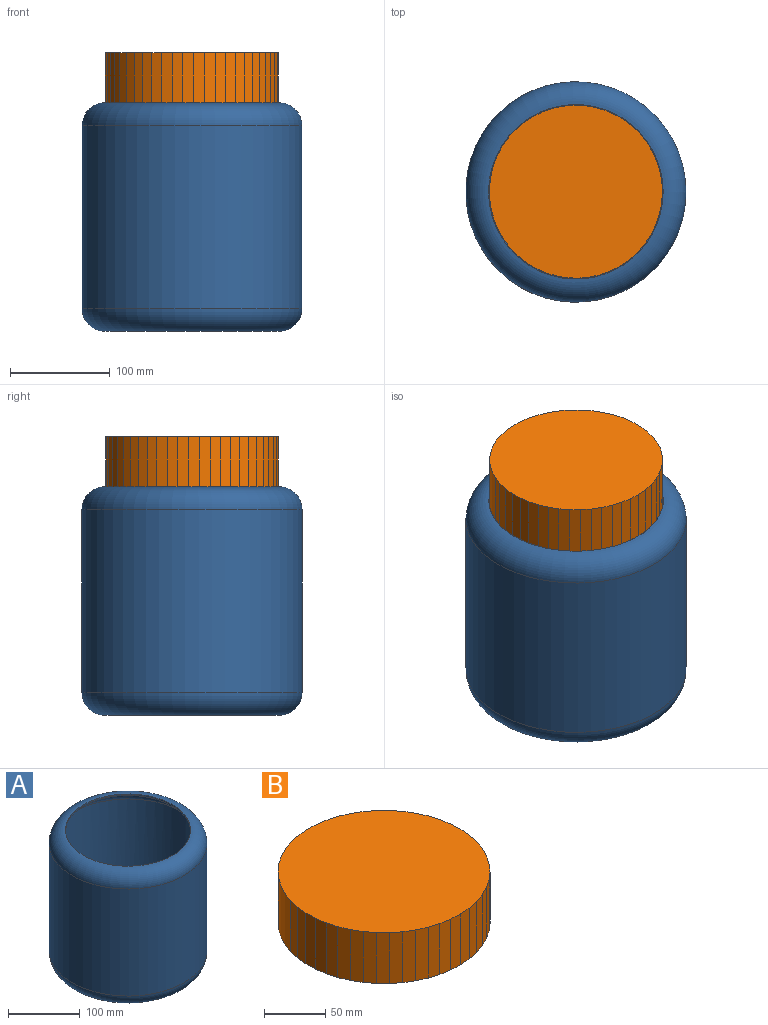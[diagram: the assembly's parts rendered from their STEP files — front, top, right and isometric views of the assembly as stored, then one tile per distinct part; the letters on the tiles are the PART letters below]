
ASSEMBLY  parts=2 mates=1
PART A: 9 faces, bbox 238.4x238.4x228.6 mm
  f0: cylinder r=110.11mm len=220.23mm, axis (0,0,-1), area 126529.7mm2, adj f2,f3
  f1: plane 174.51x174.51mm, normal (0,0,-1), area 23918.3mm2, adj f3
  f2: torus R=87.25mm, axis (0,0,1), area 22969.9mm2, adj f0,f4
  f3: torus R=87.25mm, axis (0,0,1), area 22969.9mm2, adj f0,f1
  f4: cylinder r=87.25mm len=174.51mm, axis (0,0,1), area 1392.5mm2, adj f2,f7
  f5: cylinder r=107.57mm len=215.15mm, axis (0,0,-1), area 123611.1mm2, adj f7,f8
  f6: plane 174.51x174.51mm, normal (0,0,1), area 23918.3mm2, adj f8
  f7: torus R=87.25mm, axis (0,0,1), area 20093.4mm2, adj f4,f5
  f8: torus R=87.25mm, axis (0,0,1), area 20093.4mm2, adj f5,f6
PART B: 52 faces, bbox 172.9x173x50.8 mm
  f0: plane 50.8x9.63mm, normal (0.89,-0.46,0), area 551.9mm2, adj f1,f49,f50,f51
  f1: plane 50.8x10.18mm, normal (0.94,-0.35,0), area 551.9mm2, adj f0,f2,f50,f51
  f2: plane 50.8x10.58mm, normal (0.97,-0.23,0), area 551.9mm2, adj f1,f3,f50,f51
  f3: plane 50.8x10.81mm, normal (0.99,-0.1,0), area 551.9mm2, adj f2,f4,f50,f51
  f4: plane 50.8x10.86mm, normal (1,0.02,0), area 551.9mm2, adj f3,f5,f50,f51
  f5: plane 50.8x10.75mm, normal (0.99,0.15,0), area 551.9mm2, adj f4,f6,f50,f51
  f6: plane 50.8x10.46mm, normal (0.96,0.27,0), area 551.9mm2, adj f5,f7,f50,f51
  f7: plane 50.8x10.02mm, normal (0.92,0.39,0), area 551.9mm2, adj f6,f8,f50,f51
  f8: plane 50.8x9.41mm, normal (0.87,0.5,0), area 551.9mm2, adj f7,f9,f50,f51
  f9: plane 50.8x8.65mm, normal (0.8,0.6,0), area 551.9mm2, adj f8,f10,f50,f51
  f10: plane 50.8x7.76mm, normal (0.71,0.7,0), area 551.9mm2, adj f9,f11,f50,f51
  f11: plane 50.8x8.52mm, normal (0.62,0.78,0), area 551.9mm2, adj f10,f12,f50,f51
  f12: plane 50.8x9.3mm, normal (0.52,0.86,0), area 551.9mm2, adj f11,f13,f50,f51
  f13: plane 50.8x9.93mm, normal (0.41,0.91,0), area 551.9mm2, adj f12,f14,f50,f51
  f14: plane 50.8x10.4mm, normal (0.29,0.96,0), area 551.9mm2, adj f13,f15,f50,f51
  f15: plane 50.8x10.71mm, normal (0.17,0.99,0), area 551.9mm2, adj f14,f16,f50,f51
  f16: plane 50.8x10.86mm, normal (0.04,1,0), area 551.9mm2, adj f15,f17,f50,f51
  f17: plane 50.8x10.83mm, normal (-0.08,1,0), area 551.9mm2, adj f16,f18,f50,f51
  f18: plane 50.8x10.63mm, normal (-0.21,0.98,0), area 551.9mm2, adj f17,f19,f50,f51
  f19: plane 50.8x10.26mm, normal (-0.33,0.94,0), area 551.9mm2, adj f18,f20,f50,f51
  f20: plane 50.8x9.73mm, normal (-0.44,0.9,0), area 551.9mm2, adj f19,f21,f50,f51
  f21: plane 50.8x9.05mm, normal (-0.55,0.83,0), area 551.9mm2, adj f20,f22,f50,f51
  f22: plane 50.8x8.22mm, normal (-0.65,0.76,0), area 551.9mm2, adj f21,f23,f50,f51
  f23: plane 50.8x8.08mm, normal (-0.74,0.67,0), area 551.9mm2, adj f22,f24,f50,f51
  f24: plane 50.8x8.92mm, normal (-0.82,0.57,0), area 551.9mm2, adj f23,f25,f50,f51
  f25: plane 50.8x9.63mm, normal (-0.89,0.46,0), area 551.9mm2, adj f24,f26,f50,f51
  f26: plane 50.8x10.18mm, normal (-0.94,0.35,0), area 551.9mm2, adj f25,f27,f50,f51
  f27: plane 50.8x10.58mm, normal (-0.97,0.23,0), area 551.9mm2, adj f26,f28,f50,f51
  f28: plane 50.8x10.81mm, normal (-0.99,0.1,0), area 551.9mm2, adj f27,f29,f50,f51
  f29: plane 50.8x10.86mm, normal (-1,-0.02,0), area 551.9mm2, adj f28,f30,f50,f51
  f30: plane 50.8x10.75mm, normal (-0.99,-0.15,0), area 551.9mm2, adj f29,f31,f50,f51
  f31: plane 50.8x10.46mm, normal (-0.96,-0.27,0), area 551.9mm2, adj f30,f32,f50,f51
  f32: plane 50.8x10.02mm, normal (-0.92,-0.39,0), area 551.9mm2, adj f31,f33,f50,f51
  f33: plane 50.8x9.41mm, normal (-0.87,-0.5,0), area 551.9mm2, adj f32,f34,f50,f51
  f34: plane 50.8x8.65mm, normal (-0.8,-0.6,0), area 551.9mm2, adj f33,f35,f50,f51
  f35: plane 50.8x7.76mm, normal (-0.71,-0.7,0), area 551.9mm2, adj f34,f36,f50,f51
  f36: plane 50.8x8.52mm, normal (-0.62,-0.78,0), area 551.9mm2, adj f35,f37,f50,f51
  f37: plane 50.8x9.3mm, normal (-0.52,-0.86,0), area 551.9mm2, adj f36,f38,f50,f51
  f38: plane 50.8x9.93mm, normal (-0.41,-0.91,0), area 551.9mm2, adj f37,f39,f50,f51
  f39: plane 50.8x10.4mm, normal (-0.29,-0.96,0), area 551.9mm2, adj f38,f40,f50,f51
  f40: plane 50.8x10.71mm, normal (-0.17,-0.99,0), area 551.9mm2, adj f39,f41,f50,f51
  f41: plane 50.8x10.86mm, normal (-0.04,-1,0), area 551.9mm2, adj f40,f42,f50,f51
  f42: plane 50.8x10.83mm, normal (0.08,-1,0), area 551.9mm2, adj f41,f43,f50,f51
  f43: plane 50.8x10.63mm, normal (0.21,-0.98,0), area 551.9mm2, adj f42,f44,f50,f51
  f44: plane 50.8x10.26mm, normal (0.33,-0.94,0), area 551.9mm2, adj f43,f45,f50,f51
  f45: plane 50.8x9.73mm, normal (0.44,-0.9,0), area 551.9mm2, adj f44,f46,f50,f51
  f46: plane 50.8x9.05mm, normal (0.55,-0.83,0), area 551.9mm2, adj f45,f47,f50,f51
  f47: plane 50.8x8.22mm, normal (0.65,-0.76,0), area 551.9mm2, adj f46,f48,f50,f51
  f48: plane 50.8x8.08mm, normal (0.74,-0.67,0), area 551.9mm2, adj f47,f49,f50,f51
  f49: plane 50.8x8.92mm, normal (0.82,-0.57,0), area 551.9mm2, adj f0,f48,f50,f51
  f50: plane 173x172.89mm, normal (0,0,1), area 23454.5mm2, adj f0,f1,f2,f3,f4,f5,f6,f7
  f51: plane 173x172.89mm, normal (0,0,-1), area 23454.5mm2, adj f0,f1,f2,f3,f4,f5,f6,f7
PLACE A t=(-109.57,9.44,-134.58)mm
PLACE B t=(-109.57,9.44,4.49)mm
MATE slider A.f0 <-> B.f50  axis (0,0,-1) through (-109.57,9.44,-43.14)mm
